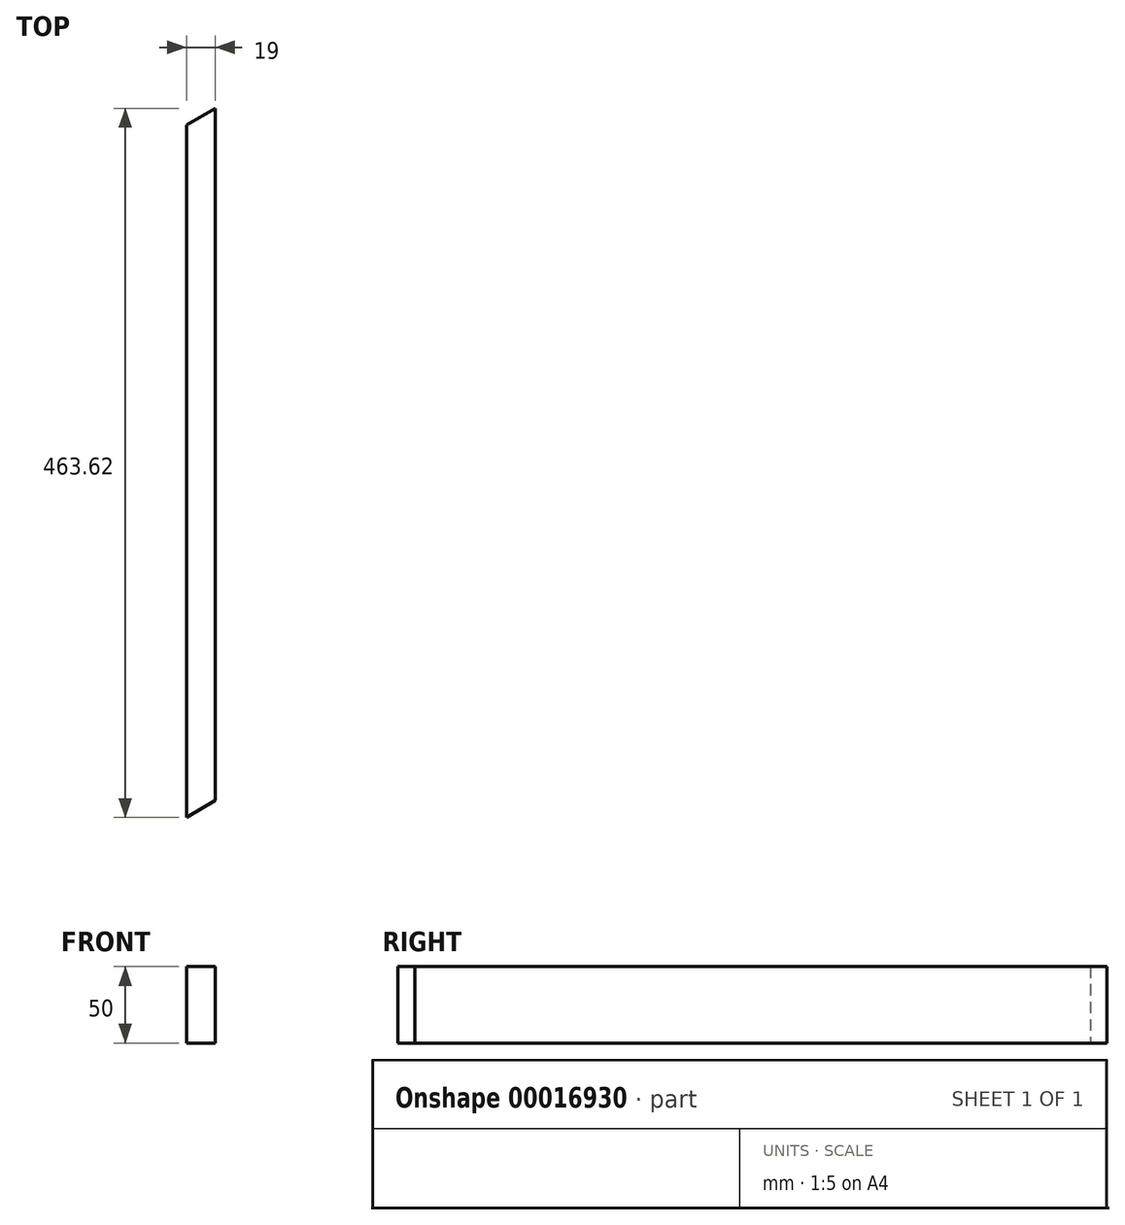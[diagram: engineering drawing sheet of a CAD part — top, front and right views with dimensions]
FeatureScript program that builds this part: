
annotation { "Feature Type Name" : "Feature", "Feature Type Description" : "" }
export const myFeature = defineFeature(function(context is Context, id is Id, definition is map)
    precondition{}
    {
        {
            var Q0;
            Q0=qCreatedBy(makeId("Top.planeOp"),FACE);
            var sketch = newSketch(context, id + "F0", { "sketchPlane" : qUnion([Q0])});
            skLineSegment(sketch, "E0.rect.left", {"start": v(9.5, -220.84) * mm, "end": v(9.5, 231.8) * mm});
            skLineSegment(sketch, "E0.rect.right", {"start": v(-9.5, -231.8) * mm, "end": v(-9.5, 220.84) * mm});
            skPoint(sketch, "E0.rect.middle", {"position": v(0, 0) * mm});
            skLineSegment(sketch, "E1", {"start": v(-9.5, 220.84) * mm, "end": v(9.5, 231.8) * mm});
            skLineSegment(sketch, "E2", {"start": v(-9.5, -231.8) * mm, "end": v(9.5, -220.84) * mm});
            skPoint(sketch, "E3.orphan", {"position": v(9.5, 231.8) * mm});
            skLineSegment(sketch, "E4", {"start": v(9.5, 231.8) * mm, "end": v(-9.5, -231.8) * mm, "construction": true});
            skSolve(sketch);
        }
        {
            var Q0;
            Q0=qSketchRegion(id+"F0",true);
            extrude(context, id + "F1", {"entities" : qUnion([Q0]), "depth" : 50 * mm});
        }
    });
